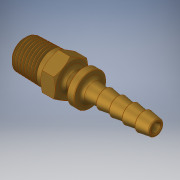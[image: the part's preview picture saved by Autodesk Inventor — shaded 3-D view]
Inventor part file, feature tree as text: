
AUTODESK INVENTOR PART (.ipt)
format: ipt  version: 2018 (Build 220112000, 112)  size: 754,688 bytes
history: native  units: in
note: dims shown in document units (in); Inventor stores cm internally (conversion verified against a paired STEP export)
features: extrude x1
ambient origin geometry x8: Origin, YZ Plane, XZ Plane, XY Plane, X Axis, Y Axis, Z Axis, Center Point
bodies: Solid1 (feature_tree)
feature tree (1):
  extrude  "Extrude1"  [1 undecoded]
note: 1 required parameter value undecoded (feature->parameter linkage not recoverable at this tier; creation-order binding heuristic only, values carry confidence <= 0.55)
